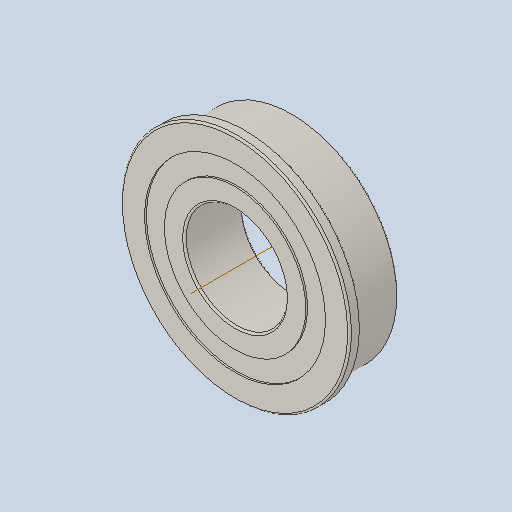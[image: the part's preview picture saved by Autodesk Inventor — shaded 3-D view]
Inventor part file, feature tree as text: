
AUTODESK INVENTOR PART (.ipt)
format: ipt  version: 2022.3 (Build 263350000, 350)  size: 210,944 bytes
history: native  units: in
note: dims shown in document units (in); Inventor stores cm internally (conversion verified against a paired STEP export)
features: other x1, revolve x1, sketch x1, fillet x1
ambient origin geometry x8: Origin, YZ Plane, XZ Plane, XY Plane, X Axis, Y Axis, Z Axis, Center Point
bodies: Solid1 (feature_tree)
feature tree (4):
  other  "Work Axis1"
  revolve  "Revolution1"  [1 undecoded]
  sketch  "Sketch1"  dims[d0=90.0deg]
  fillet  "Fillet1"  [1 undecoded]
note: 2 required parameter values undecoded (feature->parameter linkage not recoverable at this tier; creation-order binding heuristic only, values carry confidence <= 0.55)
